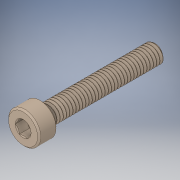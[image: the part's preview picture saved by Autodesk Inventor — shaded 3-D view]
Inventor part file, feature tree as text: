
AUTODESK INVENTOR PART (.ipt)
format: ipt  version: 2019 (Build 230136000, 136)  size: 614,400 bytes
history: mixed  units: mm
features: chamfer x1, imported_body x1
ambient origin geometry x8: Origin, YZ Plane, XZ Plane, XY Plane, X Axis, Y Axis, Z Axis, Center Point
bodies: Solid1 (imported_parasolid)
feature tree (2):
  chamfer  "Chamfer1"  [1 undecoded]
  imported_body  NMx_Import_Brep_tag  [imported B-rep: ~3 faces, bbox_mm=None]
note: 1 required parameter value undecoded (feature->parameter linkage not recoverable at this tier; creation-order binding heuristic only, values carry confidence <= 0.55)
